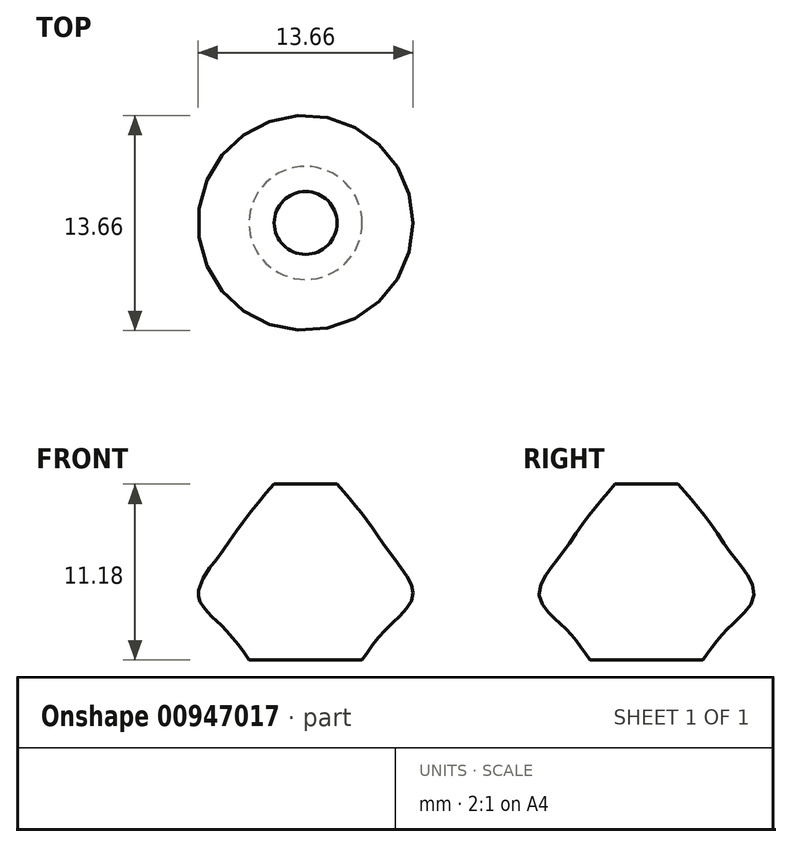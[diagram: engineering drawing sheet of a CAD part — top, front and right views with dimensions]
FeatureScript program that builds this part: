
annotation { "Feature Type Name" : "Feature", "Feature Type Description" : "" }
export const myFeature = defineFeature(function(context is Context, id is Id, definition is map)
    precondition{}
    {
        {
            var Q0;
            Q0=qCreatedBy(makeId("Top.planeOp"),FACE);
            var sketch = newSketch(context, id + "F0", { "sketchPlane" : qUnion([Q0])});
            skCircle(sketch, "E0", {"center": v(0, 0) * mm, "radius": 3.59 * mm});
            skSolve(sketch);
        }
        {
            var Q0;
            Q0=qCreatedBy(makeId("Top.planeOp"),FACE);
            cPlane(context, id + "F1", {"entities" : qUnion([Q0]), "cplaneType" : CPlaneType.OFFSET, "offset" : 2.03 * mm, "width" : 152.4 * mm, "height" : 152.4 * mm});
        }
        {
            var Q0;
            Q0=qCreatedBy(id+"F1.planeOp",FACE);
            cPlane(context, id + "F2", {"entities" : qUnion([Q0]), "cplaneType" : CPlaneType.OFFSET, "offset" : 2.03 * mm, "width" : 152.4 * mm, "height" : 152.4 * mm});
        }
        {
            var Q0;
            Q0=qCreatedBy(id+"F2.planeOp",FACE);
            cPlane(context, id + "F3", {"entities" : qUnion([Q0]), "cplaneType" : CPlaneType.OFFSET, "offset" : 2.54 * mm, "width" : 152.4 * mm, "height" : 152.4 * mm});
        }
        {
            var Q0;
            Q0=qCreatedBy(id+"F3.planeOp",FACE);
            cPlane(context, id + "F4", {"entities" : qUnion([Q0]), "cplaneType" : CPlaneType.OFFSET, "offset" : 2.3 * mm, "width" : 152.4 * mm, "height" : 152.4 * mm});
        }
        {
            var Q0;
            Q0=qCreatedBy(id+"F4.planeOp",FACE);
            cPlane(context, id + "F5", {"entities" : qUnion([Q0]), "cplaneType" : CPlaneType.OFFSET, "offset" : 2.3 * mm, "width" : 152.4 * mm, "height" : 152.4 * mm});
        }
        {
            var Q0;
            Q0=qCreatedBy(id+"F5.planeOp",FACE);
            cPlane(context, id + "F6", {"entities" : qUnion([Q0]), "cplaneType" : CPlaneType.OFFSET, "offset" : 2.54 * mm, "width" : 152.4 * mm, "height" : 152.4 * mm});
        }
        {
            var Q0;
            Q0=qCreatedBy(id+"F1.planeOp",FACE);
            var sketch = newSketch(context, id + "F7", { "sketchPlane" : qUnion([Q0])});
            skCircle(sketch, "E1", {"center": v(0, 0) * mm, "radius": 5.19 * mm});
            skSolve(sketch);
        }
        {
            var Q0;
            Q0=qCreatedBy(id+"F6.planeOp",FACE);
            cPlane(context, id + "F8", {"entities" : qUnion([Q0]), "cplaneType" : CPlaneType.OFFSET, "offset" : 1.78 * mm, "width" : 152.4 * mm, "height" : 152.4 * mm});
        }
        {
            var Q0;
            Q0=qCreatedBy(id+"F2.planeOp",FACE);
            var sketch = newSketch(context, id + "F9", { "sketchPlane" : qUnion([Q0])});
            skCircle(sketch, "E2", {"center": v(0, 0) * mm, "radius": 6.82 * mm});
            skSolve(sketch);
        }
        {
            var Q0;
            Q0=qCreatedBy(id+"F3.planeOp",FACE);
            var sketch = newSketch(context, id + "F10", { "sketchPlane" : qUnion([Q0])});
            skCircle(sketch, "E3", {"center": v(0, 0) * mm, "radius": 5.5 * mm});
            skSolve(sketch);
        }
        {
            var Q0;
            Q0=qCreatedBy(id+"F4.planeOp",FACE);
            var sketch = newSketch(context, id + "F11", { "sketchPlane" : qUnion([Q0])});
            skCircle(sketch, "E4", {"center": v(0, 0) * mm, "radius": 3.89 * mm});
            skSolve(sketch);
        }
        {
            var Q0;
            Q0=qCreatedBy(id+"F5.planeOp",FACE);
            var sketch = newSketch(context, id + "F12", { "sketchPlane" : qUnion([Q0])});
            skCircle(sketch, "E5", {"center": v(0, 0) * mm, "radius": 2 * mm});
            skSolve(sketch);
        }
        {
            var Q0;
            Q0=makeQuery(id+"F0.imprint","IMPRINT",FACE,{"disambiguationData":[TD([[makeQuery(id+"F0.imprint","IMPRINT",EDGE,{"derivedFrom":sQuery(id+"F0.wireOp",EDGE,"E0")}),1.0]])]});
            var Q1;
            Q1=makeQuery(id+"F7.imprint","IMPRINT",FACE,{"disambiguationData":[TD([[makeQuery(id+"F7.imprint","IMPRINT",EDGE,{"derivedFrom":sQuery(id+"F7.wireOp",EDGE,"E1")}),1.0]])]});
            var Q2;
            Q2=makeQuery(id+"F9.imprint","IMPRINT",FACE,{"disambiguationData":[TD([[makeQuery(id+"F9.imprint","IMPRINT",EDGE,{"derivedFrom":sQuery(id+"F9.wireOp",EDGE,"E2")}),1.0]])]});
            var Q3;
            Q3=makeQuery(id+"F10.imprint","IMPRINT",FACE,{"disambiguationData":[TD([[makeQuery(id+"F10.imprint","IMPRINT",EDGE,{"derivedFrom":sQuery(id+"F10.wireOp",EDGE,"E3")}),1.0]])]});
            var Q4;
            Q4=makeQuery(id+"F11.imprint","IMPRINT",FACE,{"disambiguationData":[TD([[makeQuery(id+"F11.imprint","IMPRINT",EDGE,{"derivedFrom":sQuery(id+"F11.wireOp",EDGE,"E4")}),1.0]])]});
            var Q5;
            Q5=makeQuery(id+"F12.imprint","IMPRINT",FACE,{"disambiguationData":[TD([[makeQuery(id+"F12.imprint","IMPRINT",EDGE,{"derivedFrom":sQuery(id+"F12.wireOp",EDGE,"E5")}),1.0]])]});
            loft(context, id + "F13", {"sheetProfilesArray" : [{ "sheetProfileEntities" : qUnion([Q0]) }, { "sheetProfileEntities" : qUnion([Q1]) }, { "sheetProfileEntities" : qUnion([Q2]) }, { "sheetProfileEntities" : qUnion([Q3]) }, { "sheetProfileEntities" : qUnion([Q4]) }, { "sheetProfileEntities" : qUnion([Q5]) }]});
        }
    });
